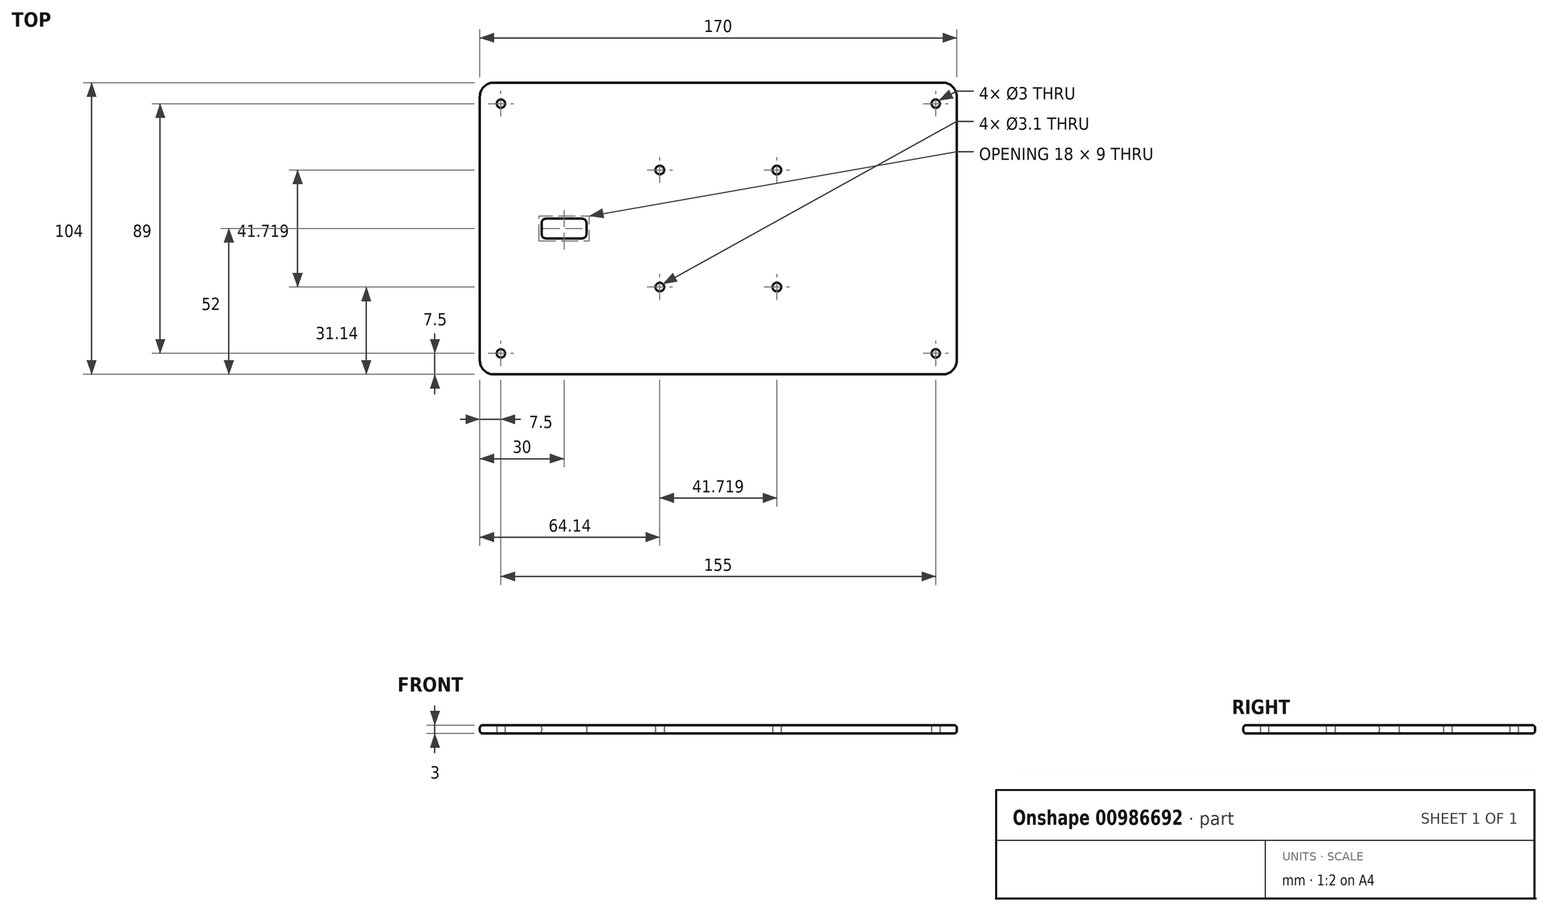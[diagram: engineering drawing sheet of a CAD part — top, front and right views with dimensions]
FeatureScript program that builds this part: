
annotation { "Feature Type Name" : "Feature", "Feature Type Description" : "" }
export const myFeature = defineFeature(function(context is Context, id is Id, definition is map)
    precondition{}
    {
        {
            var Q0;
            Q0=qCreatedBy(makeId("Top.planeOp"),FACE);
            var sketch = newSketch(context, id + "F0", { "sketchPlane" : qUnion([Q0])});
            skCircle(sketch, "E0", {"center": v(-77.5, 44.5) * mm, "radius": 1.5 * mm});
            skCircle(sketch, "E1.MirrorC", {"center": v(77.5, 44.5) * mm, "radius": 1.5 * mm});
            skCircle(sketch, "E2.MirrorC", {"center": v(-77.5, -44.5) * mm, "radius": 1.5 * mm});
            skCircle(sketch, "E3.MirrorC", {"center": v(77.5, -44.5) * mm, "radius": 1.5 * mm});
            skLineSegment(sketch, "E4.bottom", {"start": v(-85, 52) * mm, "end": v(85, 52) * mm});
            skLineSegment(sketch, "E4.top", {"start": v(-85, -52) * mm, "end": v(85, -52) * mm});
            skLineSegment(sketch, "E4.left", {"start": v(-85, 52) * mm, "end": v(-85, -52) * mm});
            skLineSegment(sketch, "E4.right", {"start": v(85, 52) * mm, "end": v(85, -52) * mm});
            skCircle(sketch, "E5", {"center": v(0, 0) * mm, "radius": 29.5 * mm, "construction": true});
            skCircle(sketch, "E6", {"center": v(-20.86, 20.86) * mm, "radius": 1.55 * mm});
            skCircle(sketch, "E7.1.0", {"center": v(-20.86, -20.86) * mm, "radius": 1.55 * mm});
            skCircle(sketch, "E7.2.0", {"center": v(20.86, -20.86) * mm, "radius": 1.55 * mm});
            skCircle(sketch, "E7.3.0", {"center": v(20.86, 20.86) * mm, "radius": 1.55 * mm});
            skCircle(sketch, "E8", {"center": v(0, 0) * mm, "radius": 37.5 * mm, "construction": true});
            skLineSegment(sketch, "E9.bottom", {"start": v(-63, -3.5) * mm, "end": v(-47, -3.5) * mm});
            skLineSegment(sketch, "E9.top", {"start": v(-63, 3.5) * mm, "end": v(-47, 3.5) * mm});
            skLineSegment(sketch, "E9.left", {"start": v(-63, -3.5) * mm, "end": v(-63, 3.5) * mm});
            skLineSegment(sketch, "E9.right", {"start": v(-47, -3.5) * mm, "end": v(-47, 3.5) * mm});
            skPoint(sketch, "E9.middle", {"position": v(-55, 0) * mm});
            skSolve(sketch);
        }
        {
            var Q0;
            Q0=makeQuery(id+"F0.imprint","IMPRINT",FACE,{"disambiguationData":[TD([[makeQuery(id+"F0.imprint","IMPRINT",EDGE,{"derivedFrom":sQuery(id+"F0.wireOp",EDGE,"E0")}),-1.0]])]});
            extrude(context, id + "F1", {"entities" : qUnion([Q0]), "depth" : 3 * mm});
        }
        {
            var Q0;
            Q0=makeQuery(id+"F1.opExtrude","SWEPT_EDGE",EDGE,{"disambiguationData":[OSD([sQuery(id+"F0.wireOp",EDGE,"E4.top"),sQuery(id+"F0.wireOp",EDGE,"E4.left")])]});
            var Q1;
            Q1=makeQuery(id+"F1.opExtrude","SWEPT_EDGE",EDGE,{"disambiguationData":[OSD([sQuery(id+"F0.wireOp",EDGE,"E4.bottom"),sQuery(id+"F0.wireOp",EDGE,"E4.left")])]});
            var Q2;
            Q2=makeQuery(id+"F1.opExtrude","SWEPT_EDGE",EDGE,{"disambiguationData":[OSD([sQuery(id+"F0.wireOp",EDGE,"E4.bottom"),sQuery(id+"F0.wireOp",EDGE,"E4.right")])]});
            var Q3;
            Q3=makeQuery(id+"F1.opExtrude","SWEPT_EDGE",EDGE,{"disambiguationData":[OSD([sQuery(id+"F0.wireOp",EDGE,"E4.top"),sQuery(id+"F0.wireOp",EDGE,"E4.right")])]});
            fillet(context, id + "F2", {"entities" : qUnion([Q0, Q1, Q2, Q3]), "radius" : 5 * mm, "tangentPropagation" : true, "allowEdgeOverflow" : false});
        }
        {
            var Q0;
            Q0=makeQuery(id+"F1.opExtrude","SWEPT_EDGE",EDGE,{"disambiguationData":[OSD([sQuery(id+"F0.wireOp",EDGE,"E9.top"),sQuery(id+"F0.wireOp",EDGE,"E9.right")])]});
            var Q1;
            Q1=makeQuery(id+"F1.opExtrude","SWEPT_EDGE",EDGE,{"disambiguationData":[OSD([sQuery(id+"F0.wireOp",EDGE,"E9.bottom"),sQuery(id+"F0.wireOp",EDGE,"E9.right")])]});
            var Q2;
            Q2=makeQuery(id+"F1.opExtrude","SWEPT_EDGE",EDGE,{"disambiguationData":[OSD([sQuery(id+"F0.wireOp",EDGE,"E9.bottom"),sQuery(id+"F0.wireOp",EDGE,"E9.left")])]});
            var Q3;
            Q3=makeQuery(id+"F1.opExtrude","SWEPT_EDGE",EDGE,{"disambiguationData":[OSD([sQuery(id+"F0.wireOp",EDGE,"E9.top"),sQuery(id+"F0.wireOp",EDGE,"E9.left")])]});
            fillet(context, id + "F3", {"entities" : qUnion([Q0, Q1, Q2, Q3]), "radius" : 1.5 * mm, "tangentPropagation" : true, "allowEdgeOverflow" : false});
        }
        {
            var Q0;
            Q0=makeQuery(id+"F1.opExtrude","CAP_EDGE",EDGE,{"disambiguationData":[OSD([sQuery(id+"F0.wireOp",EDGE,"E4.bottom")])],"isStart":false});
            var Q1;
            Q1=makeQuery(id+"F1.opExtrude","CAP_EDGE",EDGE,{"disambiguationData":[OSD([sQuery(id+"F0.wireOp",EDGE,"E4.bottom")])],"isStart":true});
            var Q2;
            Q2=makeQuery(id+"F1.opExtrude","CAP_EDGE",EDGE,{"disambiguationData":[OSD([sQuery(id+"F0.wireOp",EDGE,"E9.bottom")])],"isStart":false});
            var Q3;
            Q3=makeQuery(id+"F1.opExtrude","CAP_EDGE",EDGE,{"disambiguationData":[OSD([sQuery(id+"F0.wireOp",EDGE,"E9.top")])],"isStart":true});
            fillet(context, id + "F4", {"entities" : qUnion([Q0, Q1, Q2, Q3]), "radius" : 1 * mm, "tangentPropagation" : true, "allowEdgeOverflow" : false});
        }
    });
